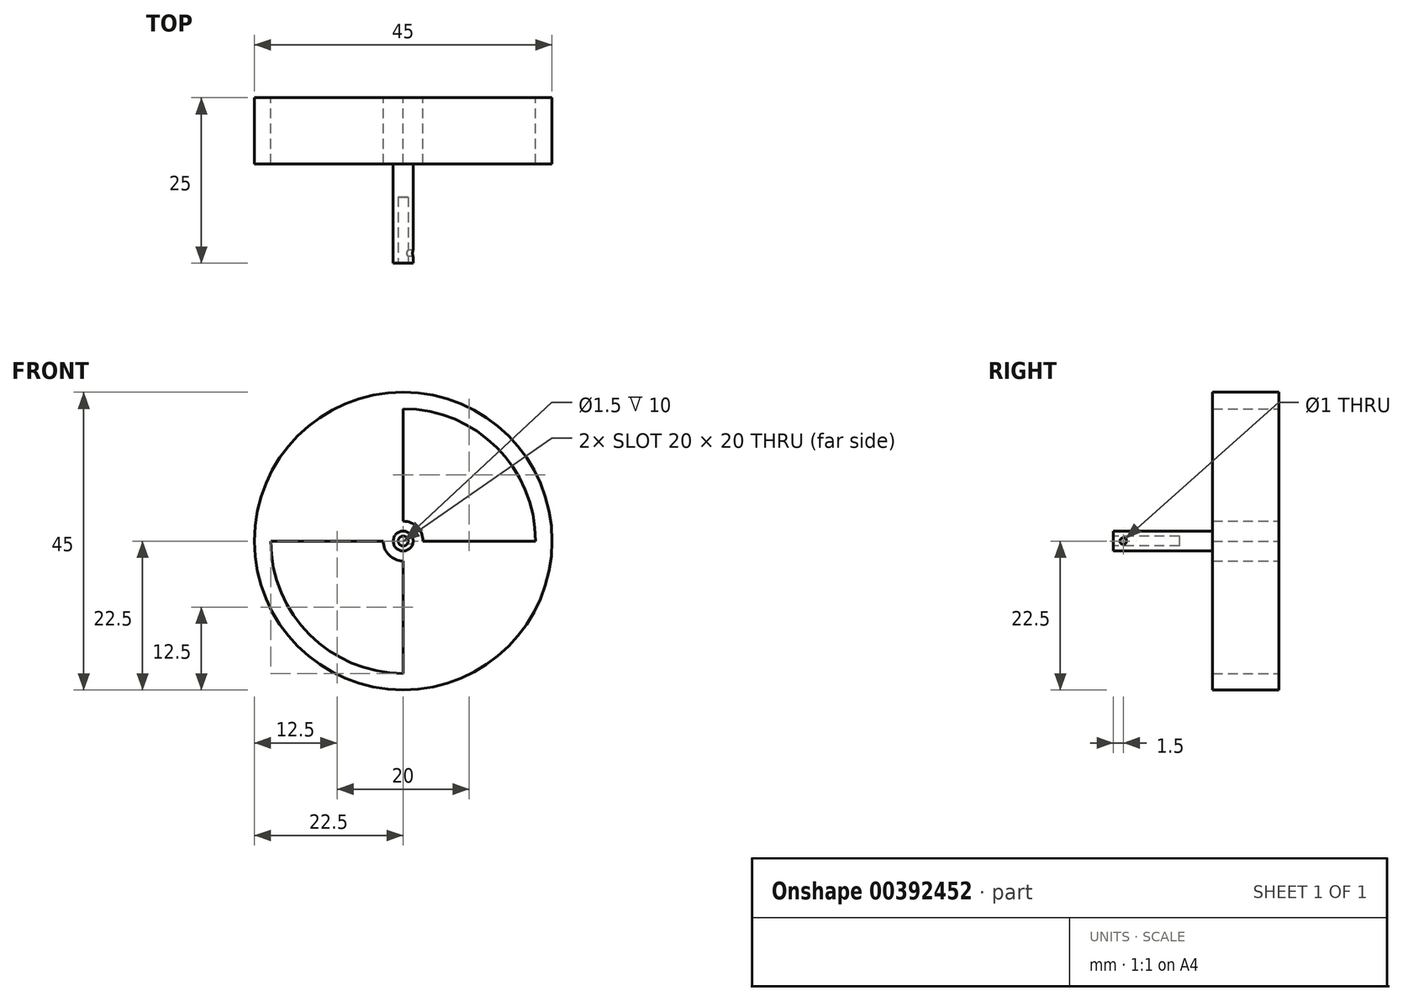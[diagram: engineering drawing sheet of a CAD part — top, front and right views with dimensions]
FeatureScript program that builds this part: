
annotation { "Feature Type Name" : "Feature", "Feature Type Description" : "" }
export const myFeature = defineFeature(function(context is Context, id is Id, definition is map)
    precondition{}
    {
        {
            var Q0;
            Q0=qCreatedBy(makeId("Front.planeOp"),FACE);
            var sketch = newSketch(context, id + "F0", { "sketchPlane" : qUnion([Q0])});
            skCircle(sketch, "E0", {"center": v(0, 0) * mm, "radius": 20 * mm});
            skLineSegment(sketch, "E1", {"start": v(0, 20) * mm, "end": v(0, 0) * mm});
            skLineSegment(sketch, "E2", {"start": v(0, 0) * mm, "end": v(20, 0) * mm});
            skLineSegment(sketch, "E3", {"start": v(0, 0) * mm, "end": v(0, -20) * mm});
            skLineSegment(sketch, "E4", {"start": v(0, 0) * mm, "end": v(-20, 0) * mm});
            skCircle(sketch, "E5", {"center": v(0, 0) * mm, "radius": 22.5 * mm});
            skCircle(sketch, "E6", {"center": v(0, 0) * mm, "radius": 3 * mm});
            skCircle(sketch, "E7", {"center": v(0, 0) * mm, "radius": 1.5 * mm});
            skSolve(sketch);
        }
        {
            var Q0;
            Q0 = qSketchRegion(id + "F0", true);
            var Q1;
            {var subQ0=sQuery(id+"F0.wireOp",EDGE,"E1");var subQ1=sQuery(id+"F0.wireOp",EDGE,"E0");var subQ2=makeQuery(id+"F0.imprint","INTERSECT",VERTEX,{"derivedFrom":[subQ1,subQ0]});Q1=makeQuery(id+"F0.imprint","IMPRINT",FACE,{"disambiguationData":[TD([[makeQuery(id+"F0.imprint","IMPRINT",EDGE,{"disambiguationData":[TD([[subQ2,-1.0]])],"derivedFrom":subQ1}),1.0]])]});}
            var Q2;
            {var subQ1=sQuery(id+"F0.wireOp",EDGE,"E1");var subQ3=sQuery(id+"F0.wireOp",EDGE,"E6");var subQ4=makeQuery(id+"F0.imprint","INTERSECT",VERTEX,{"derivedFrom":[subQ1,subQ3]});Q2=makeQuery(id+"F0.imprint","IMPRINT",FACE,{"disambiguationData":[TD([[makeQuery(id+"F0.imprint","IMPRINT",EDGE,{"disambiguationData":[TD([[subQ4,-1.0]])],"derivedFrom":subQ3}),1.0]])]});}
            var Q3;
            {var subQ1=sQuery(id+"F0.wireOp",EDGE,"E1");var subQ3=sQuery(id+"F0.wireOp",EDGE,"E6");var subQ4=makeQuery(id+"F0.imprint","INTERSECT",VERTEX,{"derivedFrom":[subQ1,subQ3]});Q3=makeQuery(id+"F0.imprint","IMPRINT",FACE,{"disambiguationData":[TD([[makeQuery(id+"F0.imprint","IMPRINT",EDGE,{"disambiguationData":[TD([[subQ4,1.0]])],"derivedFrom":subQ3}),1.0]])]});}
            var Q4;
            {var subQ1=sQuery(id+"F0.wireOp",EDGE,"E3");var subQ3=sQuery(id+"F0.wireOp",EDGE,"E6");var subQ4=makeQuery(id+"F0.imprint","INTERSECT",VERTEX,{"derivedFrom":[subQ1,subQ3]});Q4=makeQuery(id+"F0.imprint","IMPRINT",FACE,{"disambiguationData":[TD([[makeQuery(id+"F0.imprint","IMPRINT",EDGE,{"disambiguationData":[TD([[subQ4,1.0]])],"derivedFrom":subQ3}),1.0]])]});}
            var Q5;
            {var subQ1=sQuery(id+"F0.wireOp",EDGE,"E2");var subQ3=sQuery(id+"F0.wireOp",EDGE,"E6");var subQ4=makeQuery(id+"F0.imprint","INTERSECT",VERTEX,{"derivedFrom":[subQ1,subQ3]});Q5=makeQuery(id+"F0.imprint","IMPRINT",FACE,{"disambiguationData":[TD([[makeQuery(id+"F0.imprint","IMPRINT",EDGE,{"disambiguationData":[TD([[subQ4,1.0]])],"derivedFrom":subQ3}),1.0]])]});}
            var Q6;
            {var subQ0=sQuery(id+"F0.wireOp",EDGE,"E2");var subQ1=sQuery(id+"F0.wireOp",EDGE,"E0");var subQ2=makeQuery(id+"F0.imprint","INTERSECT",VERTEX,{"derivedFrom":[subQ1,subQ0]});Q6=makeQuery(id+"F0.imprint","IMPRINT",FACE,{"disambiguationData":[TD([[makeQuery(id+"F0.imprint","IMPRINT",EDGE,{"disambiguationData":[TD([[subQ2,1.0]])],"derivedFrom":subQ1}),1.0]])]});}
            extrude(context, id + "F1", {"entities" : qUnion([Q0, Q1, Q2, Q3, Q4, Q5, Q6]), "depth" : 10 * mm});
        }
        {
            var Q0;
            {var subQ1=sQuery(id+"F0.wireOp",EDGE,"E1");var subQ3=sQuery(id+"F0.wireOp",EDGE,"E7");var subQ4=makeQuery(id+"F0.imprint","INTERSECT",VERTEX,{"derivedFrom":[subQ1,subQ3]});Q0=makeQuery(id+"F0.imprint","IMPRINT",FACE,{"disambiguationData":[TD([[makeQuery(id+"F0.imprint","IMPRINT",EDGE,{"disambiguationData":[TD([[subQ4,-1.0]])],"derivedFrom":subQ3}),1.0]])]});}
            var Q1;
            {var subQ1=sQuery(id+"F0.wireOp",EDGE,"E3");var subQ3=sQuery(id+"F0.wireOp",EDGE,"E7");var subQ4=makeQuery(id+"F0.imprint","INTERSECT",VERTEX,{"derivedFrom":[subQ1,subQ3]});Q1=makeQuery(id+"F0.imprint","IMPRINT",FACE,{"disambiguationData":[TD([[makeQuery(id+"F0.imprint","IMPRINT",EDGE,{"disambiguationData":[TD([[subQ4,1.0]])],"derivedFrom":subQ3}),1.0]])]});}
            var Q2;
            {var subQ1=sQuery(id+"F0.wireOp",EDGE,"E2");var subQ3=sQuery(id+"F0.wireOp",EDGE,"E7");var subQ4=makeQuery(id+"F0.imprint","INTERSECT",VERTEX,{"derivedFrom":[subQ1,subQ3]});Q2=makeQuery(id+"F0.imprint","IMPRINT",FACE,{"disambiguationData":[TD([[makeQuery(id+"F0.imprint","IMPRINT",EDGE,{"disambiguationData":[TD([[subQ4,1.0]])],"derivedFrom":subQ3}),1.0]])]});}
            var Q3;
            {var subQ1=sQuery(id+"F0.wireOp",EDGE,"E1");var subQ3=sQuery(id+"F0.wireOp",EDGE,"E7");var subQ4=makeQuery(id+"F0.imprint","INTERSECT",VERTEX,{"derivedFrom":[subQ1,subQ3]});Q3=makeQuery(id+"F0.imprint","IMPRINT",FACE,{"disambiguationData":[TD([[makeQuery(id+"F0.imprint","IMPRINT",EDGE,{"disambiguationData":[TD([[subQ4,1.0]])],"derivedFrom":subQ3}),1.0]])]});}
            extrude(context, id + "F2", {"entities" : qUnion([Q0, Q1, Q2, Q3]), "operationType" : NewBodyOperationType.ADD, "depth" : 25 * mm});
        }
        {
            var Q0;
            Q0=makeQuery(id+"F2.opExtrude","SWEPT_FACE",FACE,{"disambiguationData":[OSD([sQuery(id+"F0.wireOp",EDGE,"E7")])]});
            cPlane(context, id + "F3", {"entities" : qUnion([Q0]), "cplaneType" : CPlaneType.LINE_ANGLE, "offset" : 25 * mm, "angle" : 90 * degree, "width" : 150 * mm, "height" : 150 * mm});
        }
        {
            var Q0;
            Q0=qCreatedBy(id+"F3.planeOp",FACE);
            var sketch = newSketch(context, id + "F4", { "sketchPlane" : qUnion([Q0])});
            skCircle(sketch, "E8", {"center": v(-23.5, 0) * mm, "radius": 0.5 * mm});
            skSolve(sketch);
        }
        {
            var Q0;
            Q0 = qSketchRegion(id + "F4", true);
            extrude(context, id + "F5", {"entities" : qUnion([Q0]), "operationType" : NewBodyOperationType.REMOVE, "depth" : 2.5 * mm});
        }
        {
            var Q0;
            Q0=makeQuery(id+"F2.opExtrude","CAP_FACE",FACE,{"disambiguationData":[OSD([sQuery(id+"F0.wireOp",EDGE,"E7")])],"isStart":false});
            var sketch = newSketch(context, id + "F6", { "sketchPlane" : qUnion([Q0])});
            skCircle(sketch, "E9", {"center": v(0, 0) * mm, "radius": 0.75 * mm});
            skSolve(sketch);
        }
        {
            var Q0;
            Q0 = qSketchRegion(id + "F6", true);
            extrude(context, id + "F7", {"entities" : qUnion([Q0]), "operationType" : NewBodyOperationType.REMOVE, "oppositeDirection" : true, "depth" : 10 * mm});
        }
    });
